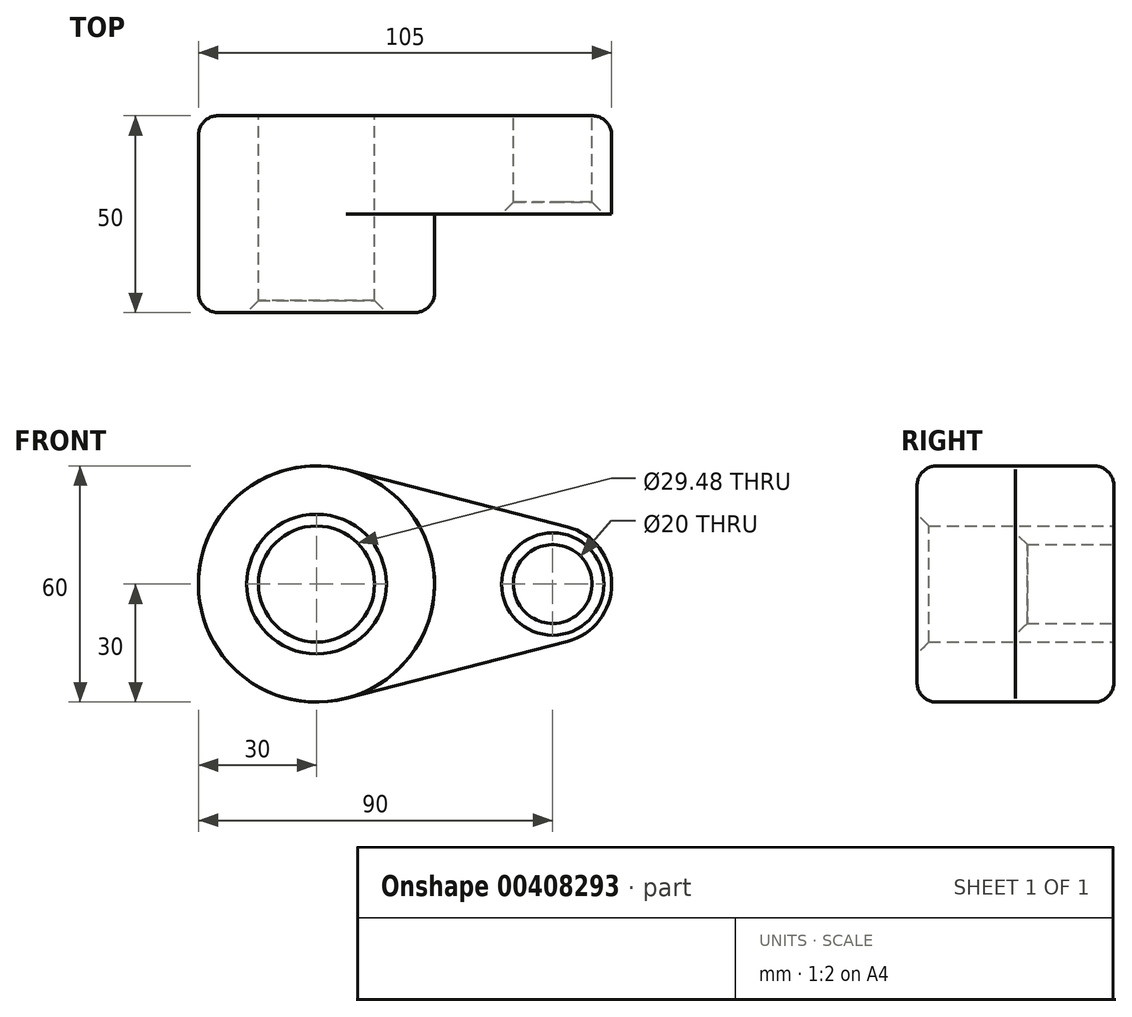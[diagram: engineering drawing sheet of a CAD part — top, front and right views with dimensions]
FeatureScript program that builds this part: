
annotation { "Feature Type Name" : "Feature", "Feature Type Description" : "" }
export const myFeature = defineFeature(function(context is Context, id is Id, definition is map)
    precondition{}
    {
        {
            var Q0;
            Q0=qCreatedBy(makeId("Front.planeOp"),FACE);
            var sketch = newSketch(context, id + "F0", { "sketchPlane" : qUnion([Q0])});
            skCircle(sketch, "E0", {"center": v(0, 0) * mm, "radius": 30 * mm});
            skCircle(sketch, "E1", {"center": v(60, 0) * mm, "radius": 15 * mm});
            skLineSegment(sketch, "E2", {"start": v(7.5, 29.05) * mm, "end": v(63.75, 14.52) * mm});
            skLineSegment(sketch, "E3", {"start": v(63.75, -14.52) * mm, "end": v(7.5, -29.05) * mm});
            skCircle(sketch, "E4", {"center": v(0, 0) * mm, "radius": 14.74 * mm});
            skCircle(sketch, "E5", {"center": v(60, 0) * mm, "radius": 10 * mm});
            skSolve(sketch);
        }
        {
            var Q0;
            Q0 = qSketchRegion(id + "F0", true);
            extrude(context, id + "F1", {"entities" : qUnion([Q0]), "depth" : 25 * mm});
        }
        {
            var Q0;
            Q0=makeQuery(id+"F0.imprint","IMPRINT",FACE,{"disambiguationData":[TD([[makeQuery(id+"F0.imprint","IMPRINT",EDGE,{"derivedFrom":sQuery(id+"F0.wireOp",EDGE,"E4")}),-1.0]])]});
            extrude(context, id + "F2", {"entities" : qUnion([Q0]), "operationType" : NewBodyOperationType.ADD, "depth" : 50 * mm});
        }
        {
            var Q0;
            Q0=makeQuery(id+"F2.opExtrude","CAP_EDGE",EDGE,{"disambiguationData":[OSD([sQuery(id+"F0.wireOp",EDGE,"E0")])],"isStart":false});
            var Q1;
            Q1=makeQuery(id+"F1.opExtrude","CAP_EDGE",EDGE,{"disambiguationData":[OSD([sQuery(id+"F0.wireOp",EDGE,"E3")])],"isStart":true});
            fillet(context, id + "F3", {"entities" : qUnion([Q0, Q1]), "radius" : 5 * mm, "tangentPropagation" : true, "allowEdgeOverflow" : false});
        }
        {
            var Q0;
            Q0=makeQuery(id+"F2.opExtrude","CAP_EDGE",EDGE,{"disambiguationData":[OSD([sQuery(id+"F0.wireOp",EDGE,"E4")])],"isStart":false});
            var Q1;
            Q1=makeQuery(id+"F1.opExtrude","CAP_EDGE",EDGE,{"disambiguationData":[OSD([sQuery(id+"F0.wireOp",EDGE,"E5")])],"isStart":false});
            chamfer(context, id + "F4", {"entities" : qUnion([Q0, Q1]), "width" : 3 * mm, "tangentPropagation" : true});
        }
    });
